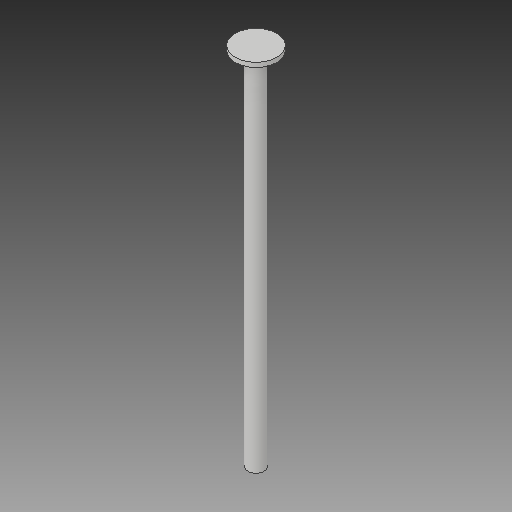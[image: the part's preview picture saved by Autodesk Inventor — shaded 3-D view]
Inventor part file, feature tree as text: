
AUTODESK INVENTOR PART (.ipt)
format: ipt  version: 2018 (Build 220112000, 112)  size: 92,672 bytes
history: native  units: in
note: dims shown in document units (in); Inventor stores cm internally (conversion verified against a paired STEP export)
features: extrude x2, sketch x2
ambient origin geometry x8: Origin, YZ Plane, XZ Plane, XY Plane, X Axis, Y Axis, Z Axis, Center Point
bodies: Solid1 (feature_tree)
feature tree (4):
  extrude  "Extrusion1"  Depth=3.3071in TaperAngle=0.0deg
  extrude  "Extrusion2"  Depth=0.0409in TaperAngle=0.0deg
  sketch  "Sketch1"  dims[d0=0.1496in d1=3.3071in d2=0.0in]
  sketch  "Sketch2"  dims[d3=0.3819in d4=0.0409in d5=0.0in]
